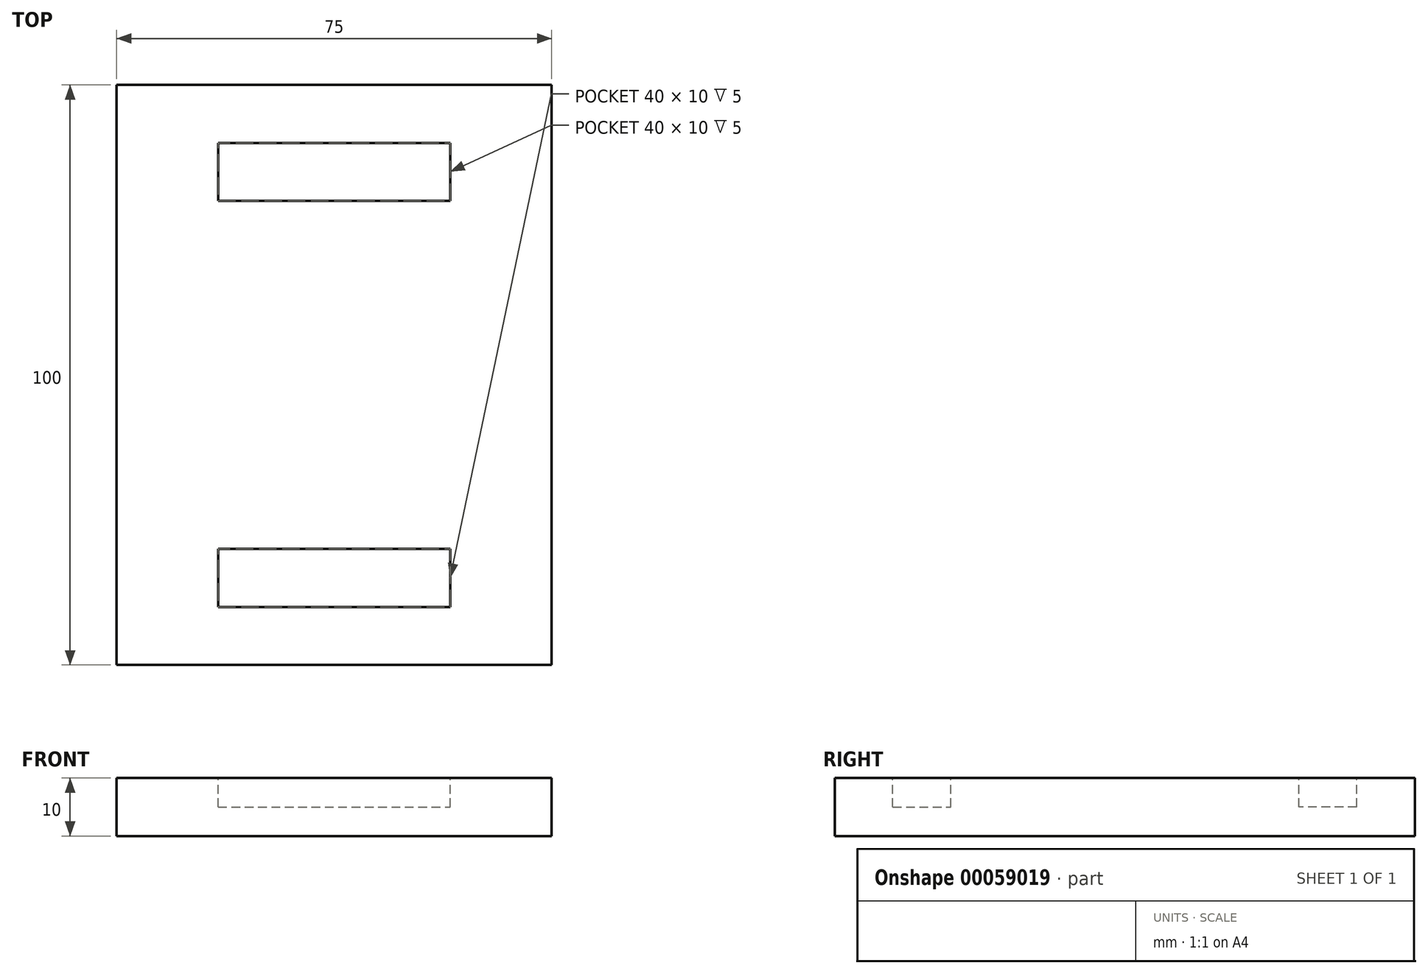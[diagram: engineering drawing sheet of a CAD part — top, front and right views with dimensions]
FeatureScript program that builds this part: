
annotation { "Feature Type Name" : "Feature", "Feature Type Description" : "" }
export const myFeature = defineFeature(function(context is Context, id is Id, definition is map)
    precondition{}
    {
        {
            var Q0;
            Q0=qCreatedBy(makeId("Top.planeOp"),FACE);
            var sketch = newSketch(context, id + "F0", { "sketchPlane" : qUnion([Q0])});
            skLineSegment(sketch, "E0.rect.bottom", {"start": v(-37.5, 50) * mm, "end": v(37.5, 50) * mm});
            skLineSegment(sketch, "E0.rect.top", {"start": v(-37.5, -50) * mm, "end": v(37.5, -50) * mm});
            skLineSegment(sketch, "E0.rect.left", {"start": v(-37.5, 50) * mm, "end": v(-37.5, -50) * mm});
            skLineSegment(sketch, "E0.rect.right", {"start": v(37.5, 50) * mm, "end": v(37.5, -50) * mm});
            skSolve(sketch);
        }
        {
            var Q0;
            Q0=makeQuery(id+"F0.imprint","IMPRINT",FACE,{"disambiguationData":[TD([[makeQuery(id+"F0.imprint","IMPRINT",EDGE,{"derivedFrom":sQuery(id+"F0.wireOp",EDGE,"E0.rect.bottom")}),-1.0]])]});
            extrude(context, id + "F1", {"entities" : qUnion([Q0]), "depth" : 10 * mm});
        }
        {
            var Q0;
            Q0=makeQuery(id+"F1.opExtrude","CAP_FACE",FACE,{"disambiguationData":[OSD([sQuery(id+"F0.wireOp",EDGE,"E0.rect.bottom"),sQuery(id+"F0.wireOp",EDGE,"E0.rect.top"),sQuery(id+"F0.wireOp",EDGE,"E0.rect.left"),sQuery(id+"F0.wireOp",EDGE,"E0.rect.right")])],"isStart":false});
            var sketch = newSketch(context, id + "F2", { "sketchPlane" : qUnion([Q0])});
            skLineSegment(sketch, "E1.rect.bottom", {"start": v(-20, 40) * mm, "end": v(20, 40) * mm});
            skLineSegment(sketch, "E1.rect.top", {"start": v(-20, 30) * mm, "end": v(20, 30) * mm});
            skLineSegment(sketch, "E1.rect.left", {"start": v(-20, 40) * mm, "end": v(-20, 30) * mm});
            skLineSegment(sketch, "E1.rect.right", {"start": v(20, 40) * mm, "end": v(20, 30) * mm});
            skPoint(sketch, "E1.rect.middle", {"position": v(0, 35) * mm});
            skLineSegment(sketch, "E2.MirrorCS", {"start": v(20, -40) * mm, "end": v(20, -30) * mm});
            skLineSegment(sketch, "E3.MirrorCS", {"start": v(-20, -40) * mm, "end": v(-20, -30) * mm});
            skLineSegment(sketch, "E4.MirrorCS", {"start": v(-20, -40) * mm, "end": v(20, -40) * mm});
            skLineSegment(sketch, "E5.MirrorCS", {"start": v(-20, -30) * mm, "end": v(20, -30) * mm});
            skPoint(sketch, "E6.MirrorP", {"position": v(0, -35) * mm});
            skSolve(sketch);
        }
        {
            var Q0;
            Q0 = qSketchRegion(id + "F2", true);
            extrude(context, id + "F3", {"entities" : qUnion([Q0]), "operationType" : NewBodyOperationType.REMOVE, "oppositeDirection" : true, "depth" : 5 * mm});
        }
    });
